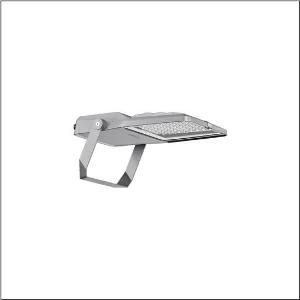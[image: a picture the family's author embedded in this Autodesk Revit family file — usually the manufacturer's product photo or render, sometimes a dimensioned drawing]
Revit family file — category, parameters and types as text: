
# Revit family: floodlight_fl_21_iq_mini___pl33t_5xa7772d1f1a_784a
name_source: partatom
category: Lighting Fixtures
units: mm (PartAtom-declared; Revit-internal decimal feet)

## family parameters
Cut with Voids When Loaded = No
Host = Face
Light Source = No
Part Type = Normal
Room Calculation Point = No
Round Connector Dimension = Use Diameter
Shared = No

## types (1)
- --- (1 x LED, 14590 lm, 143 W, 2200K)
    Apparent Load = 143 VA
    CIE Flux Codes = 26 75 99 100 100
    Color Rendering = 70
    Color Temperature = 2200K
    Default Elevation = 1800 mm
    Description = Floodlight FL 21 iQ mini, floodlight, primary light control with lens, of PMMA, primary optical cover: protective disc, of toughened safety glass, transparent, light distribution: PL33T, light emission: direct distribution, installation type: surface-mounted, lamps: LED, High Power LED, rated values: 14.590lm | 143W | 102lm/W (begin service life); end service life: 14.590lm | 151,6W; at 50% lumin. flux: 7.295lm | 60,5W | 120,6lm/W, colour temperature: 2200K, colour rendering: CRI > 70, light colour: 722, light setting 1 begin service life: 100% | 14.590lm | 143W | 102lm/W | 2.200K, light setting 1 end service life: 151,6W, further light settings possible, control: Street-Remote, Auto-Match, Temp-Guard, Night-Set, Smart-Wire, Desk-Remote (wireless, voltage-free reading and setting of iQ features in the workshop via application-optimized NFC function/RFID function), optimised constant luminous flux control (CLO 2.0), pre-setting: linear dimming characteristic, with terminal, 6-pole, mains connection: 220..240V, AC, 50/60Hz, luminaire housing, of diecast aluminium, powder-coated, SITECO metallic grey (DB 702S), corrosivity category C5 mid according to DIN EN ISO 12944suitable for swimming poolschlorine-resistant, sealing non-destructively replaceable, mounting bracket, of steel, galvanised, powder-coated, SITECO metallic grey (DB 702S), protection rating (complete): IP66, insulation class (complete): insulation class II (safety insulation), certification: CE, ENEC, VDE, protection symbol: D, impact resistance: IK08, permissible operating ambient temperature: -40..+40°C, permissible operating ambient temperature for outdoor applications: -40..+50°C, standard: DIN EN 12944, LABS conformity tested according to VDMA 24364:2018-05, packaging unit: 1 piece

Light Distribution: PL33T
    Height = 70 mm
    Lamp = 1 x LED
    Lamp Light Flux = 14590 lm
    Lamp Power = 143 W
    Lamp count = 1
    Length = 485 mm
    Luminous efficacy = 102 lm/W
    Manufacturer = Siteco
    ModVariant = No
    Model = 5XA7772D1F1A
    Mounting Place = Pole
    Mounting Type = Pole annexe
    Number of Poles = 1
    OnlyDefault = Yes
    Power Factor = 1
    Product Name = Floodlight FL 21 iQ mini | PL33T
    Product group = floodlight | pylon annexe
    ProductGroupID = 6201
    Protection Class = Protection class II
    Protection Degree = IP 66
    RLX_Detail_Level = 1
    RLX_Emergency_Light_Flux = 0 lm
    RLX_Emergency_Type = 0
    RLX_Emergency_Type_DB = No
    RlxData = <blob elided: 96521 chars, md5=653bf188>
    Socket = socket
    Standby Power = 0 W
    System Light Flux = 14590 lm
    System Power = 143 W
    Type Comments = factory setting: luminous flux: 100 % | dim-lin: 254 | 730 mA
    Type Image = l_1006845.jpg
    URL = http://relux.com
    VarID = @adj_150097
    Voltage = 0 V
    Weight = 0.00 kg
    Width = 337 mm

## geometry (parser evidence)
native form markers: Blend x4, Sweep x10
no freeform markers — native parametric forms only
